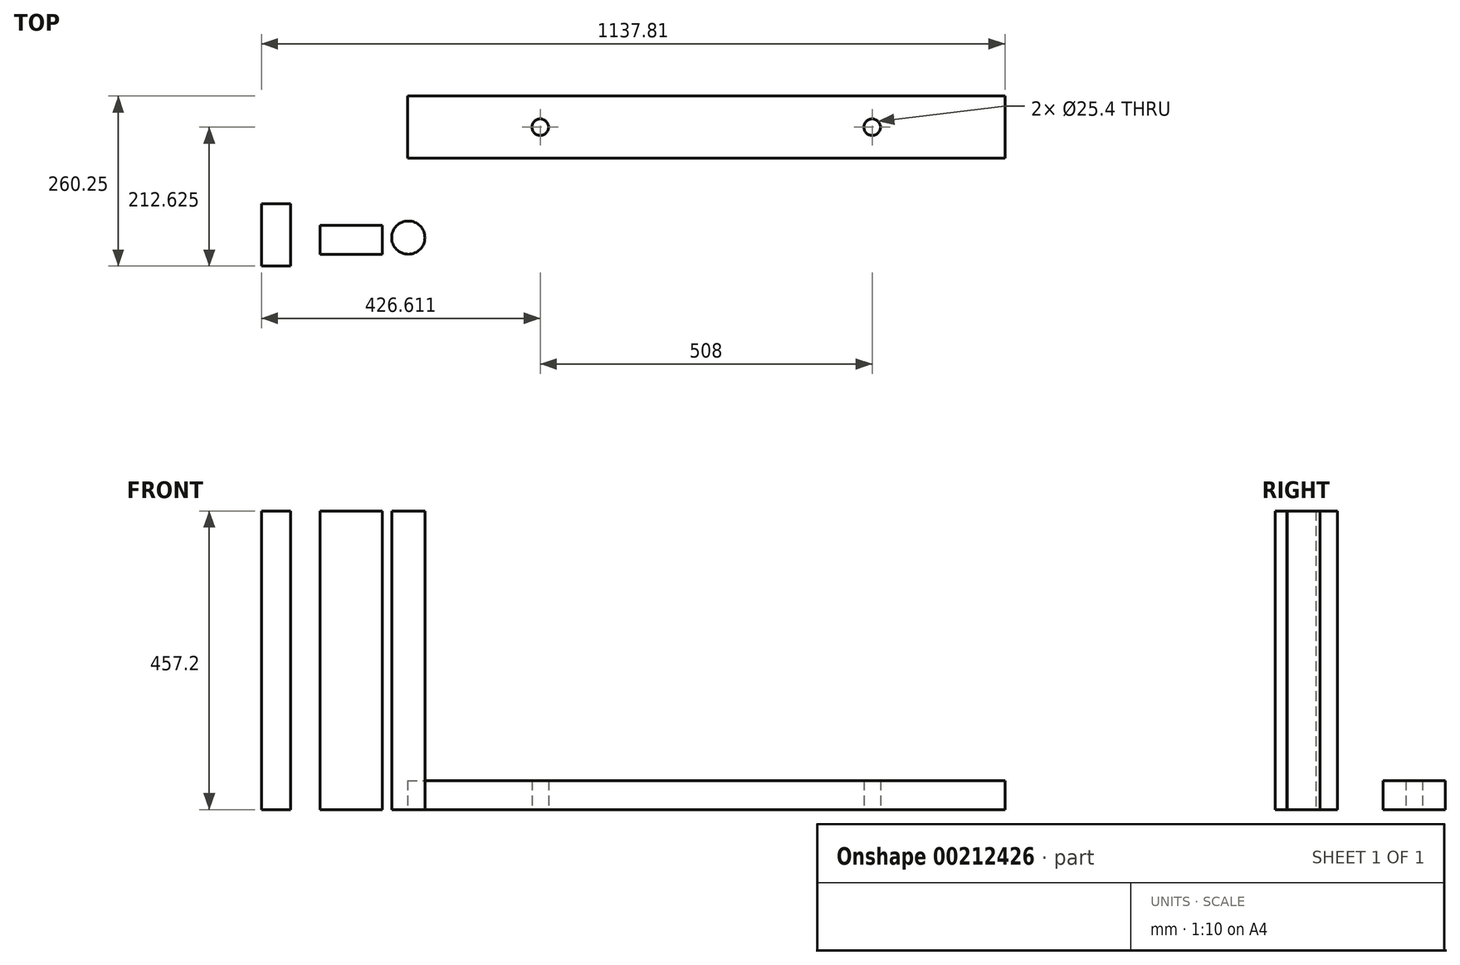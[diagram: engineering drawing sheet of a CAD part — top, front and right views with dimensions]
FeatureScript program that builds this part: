
annotation { "Feature Type Name" : "Feature", "Feature Type Description" : "" }
export const myFeature = defineFeature(function(context is Context, id is Id, definition is map)
    precondition{}
    {
        {
            var Q0;
            Q0=qCreatedBy(makeId("Top.planeOp"),FACE);
            var sketch = newSketch(context, id + "F0", { "sketchPlane" : qUnion([Q0])});
            skLineSegment(sketch, "E0.bottom", {"start": v(73.36, 140.46) * mm, "end": v(987.76, 140.46) * mm});
            skLineSegment(sketch, "E0.top", {"start": v(73.36, 45.2) * mm, "end": v(987.76, 45.2) * mm});
            skLineSegment(sketch, "E0.left", {"start": v(73.36, 140.46) * mm, "end": v(73.36, 45.2) * mm});
            skLineSegment(sketch, "E0.right", {"start": v(987.76, 140.46) * mm, "end": v(987.76, 45.2) * mm});
            skLineSegment(sketch, "E1", {"start": v(73.36, 92.83) * mm, "end": v(276.56, 92.83) * mm});
            skLineSegment(sketch, "E2", {"start": v(987.76, 45.2) * mm, "end": v(987.76, 92.83) * mm});
            skLineSegment(sketch, "E3", {"start": v(987.76, 92.83) * mm, "end": v(784.56, 92.83) * mm});
            skCircle(sketch, "E4", {"center": v(784.56, 92.83) * mm, "radius": 12.7 * mm});
            skCircle(sketch, "E5", {"center": v(276.56, 92.83) * mm, "radius": 12.7 * mm});
            skSolve(sketch);
        }
        {
            var Q0;
            Q0=makeQuery(id+"F0.imprint","IMPRINT",FACE,{"disambiguationData":[TD([[makeQuery(id+"F0.imprint","IMPRINT",EDGE,{"derivedFrom":sQuery(id+"F0.wireOp",EDGE,"E0.bottom")}),-1.0]])]});
            extrude(context, id + "F1", {"entities" : qUnion([Q0]), "depth" : 44.45 * mm});
        }
        {
            var Q0;
            Q0=qCreatedBy(makeId("Top.planeOp"),FACE);
            var sketch = newSketch(context, id + "F2", { "sketchPlane" : qUnion([Q0])});
            skLineSegment(sketch, "E6.bottom", {"start": v(-60.69, -57.68) * mm, "end": v(34.56, -57.68) * mm});
            skLineSegment(sketch, "E6.top", {"start": v(-60.69, -102.13) * mm, "end": v(34.56, -102.13) * mm});
            skLineSegment(sketch, "E6.left", {"start": v(-60.69, -57.68) * mm, "end": v(-60.69, -102.13) * mm});
            skLineSegment(sketch, "E6.right", {"start": v(34.56, -57.68) * mm, "end": v(34.56, -102.13) * mm});
            skSolve(sketch);
        }
        {
            var Q0;
            Q0=makeQuery(id+"F2.imprint","IMPRINT",FACE,{"disambiguationData":[TD([[makeQuery(id+"F2.imprint","IMPRINT",EDGE,{"derivedFrom":sQuery(id+"F2.wireOp",EDGE,"E6.bottom")}),-1.0]])]});
            extrude(context, id + "F3", {"entities" : qUnion([Q0]), "depth" : 457.2 * mm});
        }
        {
            var Q0;
            Q0=qCreatedBy(makeId("Top.planeOp"),FACE);
            var sketch = newSketch(context, id + "F4", { "sketchPlane" : qUnion([Q0])});
            skLineSegment(sketch, "E7.bottom", {"start": v(-150.05, -24.54) * mm, "end": v(-105.6, -24.54) * mm});
            skLineSegment(sketch, "E7.top", {"start": v(-150.05, -119.8) * mm, "end": v(-105.6, -119.8) * mm});
            skLineSegment(sketch, "E7.left", {"start": v(-150.05, -24.54) * mm, "end": v(-150.05, -119.8) * mm});
            skLineSegment(sketch, "E7.right", {"start": v(-105.6, -24.54) * mm, "end": v(-105.6, -119.8) * mm});
            skSolve(sketch);
        }
        {
            var Q0;
            Q0=makeQuery(id+"F4.imprint","IMPRINT",FACE,{"disambiguationData":[TD([[makeQuery(id+"F4.imprint","IMPRINT",EDGE,{"derivedFrom":sQuery(id+"F4.wireOp",EDGE,"E7.bottom")}),-1.0]])]});
            extrude(context, id + "F5", {"entities" : qUnion([Q0]), "depth" : 457.2 * mm});
        }
        {
            var Q0;
            Q0=qCreatedBy(makeId("Top.planeOp"),FACE);
            var sketch = newSketch(context, id + "F6", { "sketchPlane" : qUnion([Q0])});
            skCircle(sketch, "E8", {"center": v(74.67, -76.27) * mm, "radius": 25.4 * mm});
            skSolve(sketch);
        }
        {
            var Q0;
            Q0=makeQuery(id+"F6.imprint","IMPRINT",FACE,{"disambiguationData":[TD([[makeQuery(id+"F6.imprint","IMPRINT",EDGE,{"derivedFrom":sQuery(id+"F6.wireOp",EDGE,"E8")}),1.0]])]});
            extrude(context, id + "F7", {"entities" : qUnion([Q0]), "depth" : 457.2 * mm});
        }
    });
